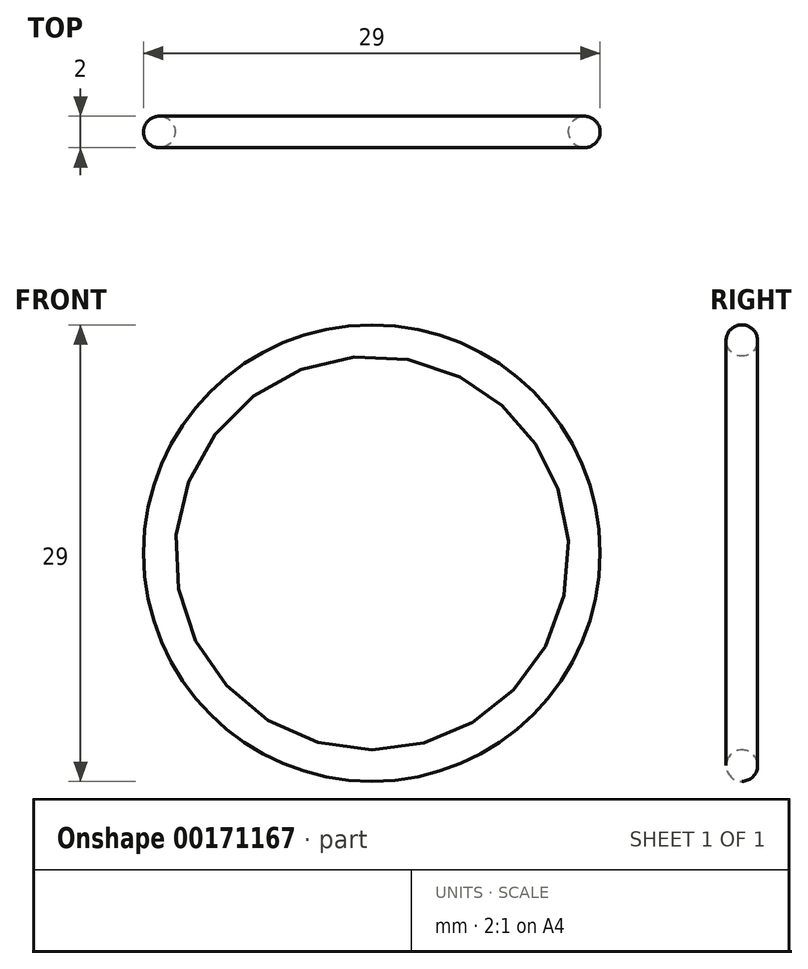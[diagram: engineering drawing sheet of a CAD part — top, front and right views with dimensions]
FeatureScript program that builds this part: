
annotation { "Feature Type Name" : "Feature", "Feature Type Description" : "" }
export const myFeature = defineFeature(function(context is Context, id is Id, definition is map)
    precondition{}
    {
        {
            var Q0;
            Q0=qCreatedBy(makeId("Front.planeOp"),FACE);
            var sketch = newSketch(context, id + "F0", { "sketchPlane" : qUnion([Q0])});
            skCircle(sketch, "E0", {"center": v(0, 0) * mm, "radius": 13.5 * mm});
            skSolve(sketch);
        }
        {
            var Q0;
            Q0=qCreatedBy(makeId("Top.planeOp"),FACE);
            var sketch = newSketch(context, id + "F1", { "sketchPlane" : qUnion([Q0])});
            skCircle(sketch, "E1", {"center": v(13.5, 0) * mm, "radius": 1 * mm});
            skSolve(sketch);
        }
        {
            var Q0;
            Q0=makeQuery(id+"F1.imprint","IMPRINT",FACE,{"disambiguationData":[TD([[makeQuery(id+"F1.imprint","IMPRINT",EDGE,{"derivedFrom":sQuery(id+"F1.wireOp",EDGE,"E1")}),1.0]])]});
            var Q1;
            Q1=sQuery(id+"F0.wireOp",EDGE,"E0");
            sweep(context, id + "F2", {"profiles" : qUnion([Q0]), "path" : qUnion([Q1])});
        }
    });
